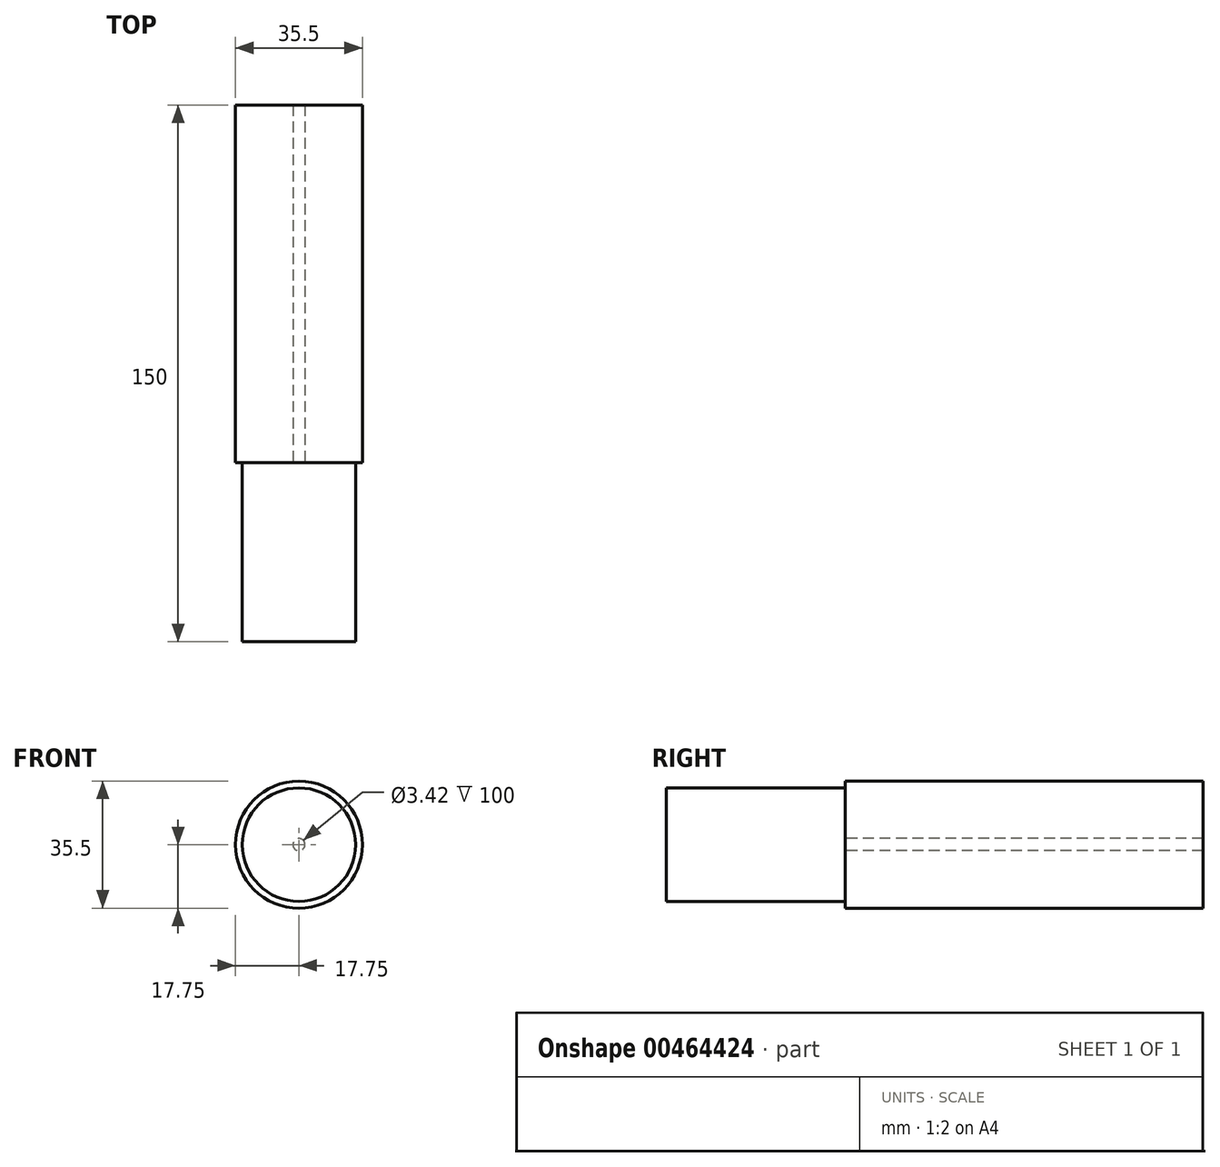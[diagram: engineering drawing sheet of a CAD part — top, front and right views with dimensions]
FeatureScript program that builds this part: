
annotation { "Feature Type Name" : "Feature", "Feature Type Description" : "" }
export const myFeature = defineFeature(function(context is Context, id is Id, definition is map)
    precondition{}
    {
        {
            var Q0;
            Q0=qCreatedBy(makeId("Front.planeOp"),FACE);
            var sketch = newSketch(context, id + "F0", { "sketchPlane" : qUnion([Q0])});
            skCircle(sketch, "E0", {"center": v(0, 0) * mm, "radius": 1.06 * mm});
            skCircle(sketch, "E1", {"center": v(0, 0) * mm, "radius": 1.71 * mm});
            skCircle(sketch, "E2", {"center": v(0, 0) * mm, "radius": 17.75 * mm});
            skSolve(sketch);
        }
        {
            var Q0;
            Q0=makeQuery(id+"F0.imprint","IMPRINT",FACE,{"disambiguationData":[TD([[makeQuery(id+"F0.imprint","IMPRINT",EDGE,{"derivedFrom":sQuery(id+"F0.wireOp",EDGE,"E1")}),-1.0]])]});
            extrude(context, id + "F1", {"entities" : qUnion([Q0]), "oppositeDirection" : true, "depth" : 100 * mm, "offsetDistance" : 25 * mm});
        }
        {
            var Q0;
            Q0=qCreatedBy(makeId("Front.planeOp"),FACE);
            var sketch = newSketch(context, id + "F2", { "sketchPlane" : qUnion([Q0])});
            skCircle(sketch, "E3", {"center": v(0, 0) * mm, "radius": 15.87 * mm});
            skSolve(sketch);
        }
        {
            var Q0;
            Q0=makeQuery(id+"F2.imprint","IMPRINT",FACE,{"disambiguationData":[TD([[makeQuery(id+"F2.imprint","IMPRINT",EDGE,{"derivedFrom":sQuery(id+"F2.wireOp",EDGE,"E3")}),1.0]])]});
            extrude(context, id + "F3", {"entities" : qUnion([Q0]), "operationType" : NewBodyOperationType.ADD, "depth" : 50 * mm, "offsetDistance" : 25 * mm});
        }
    });
